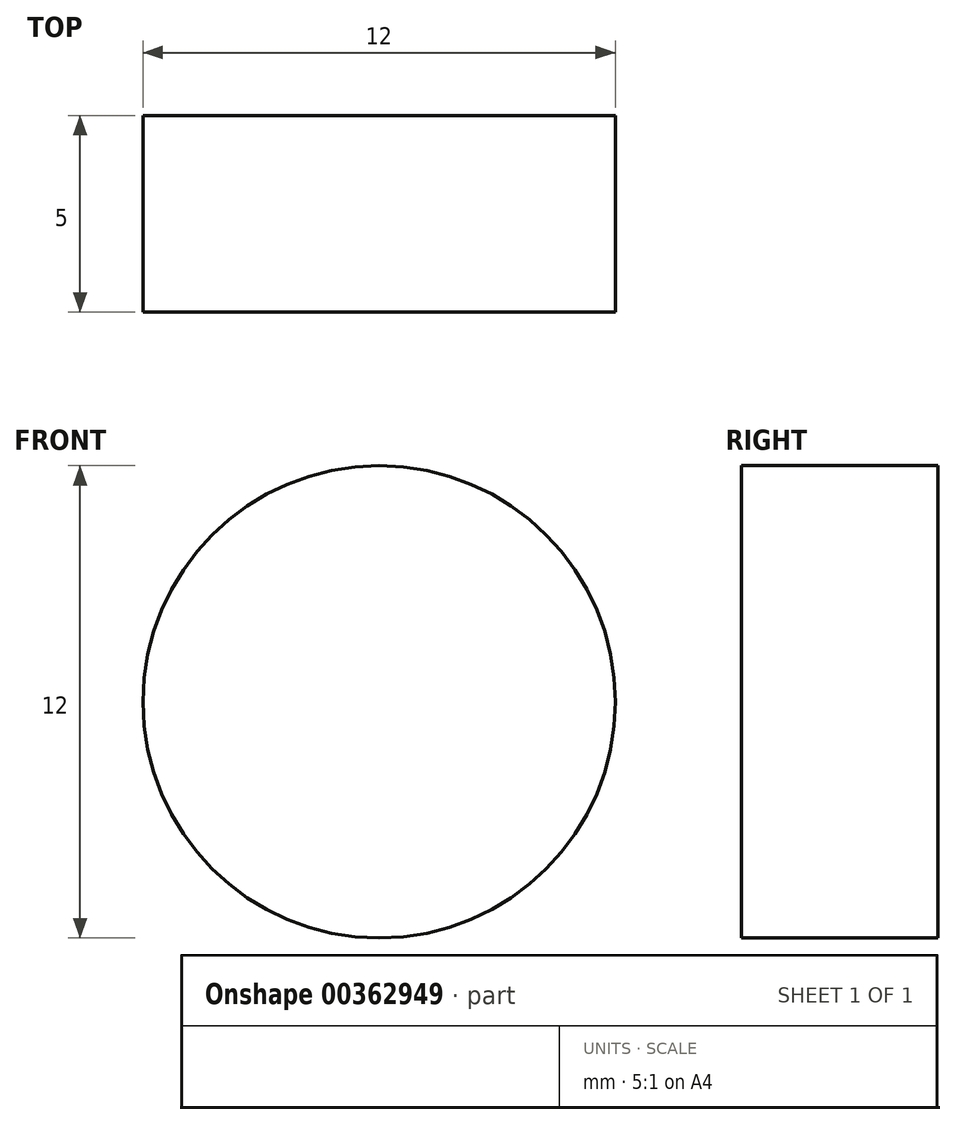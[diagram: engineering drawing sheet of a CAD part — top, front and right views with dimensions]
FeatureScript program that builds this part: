
annotation { "Feature Type Name" : "Feature", "Feature Type Description" : "" }
export const myFeature = defineFeature(function(context is Context, id is Id, definition is map)
    precondition{}
    {
        {
            var Q0;
            Q0=qCreatedBy(makeId("Front.planeOp"),FACE);
            var sketch = newSketch(context, id + "F0", { "sketchPlane" : qUnion([Q0])});
            skCircle(sketch, "E0", {"center": v(0, 0) * mm, "radius": 6 * mm});
            skSolve(sketch);
        }
        {
            var Q0;
            Q0=makeQuery(id+"F0.imprint","IMPRINT",FACE,{"disambiguationData":[TD([[makeQuery(id+"F0.imprint","IMPRINT",EDGE,{"derivedFrom":sQuery(id+"F0.wireOp",EDGE,"E0")}),1.0]])]});
            extrude(context, id + "F1", {"entities" : qUnion([Q0]), "depth" : 5 * mm});
        }
    });
